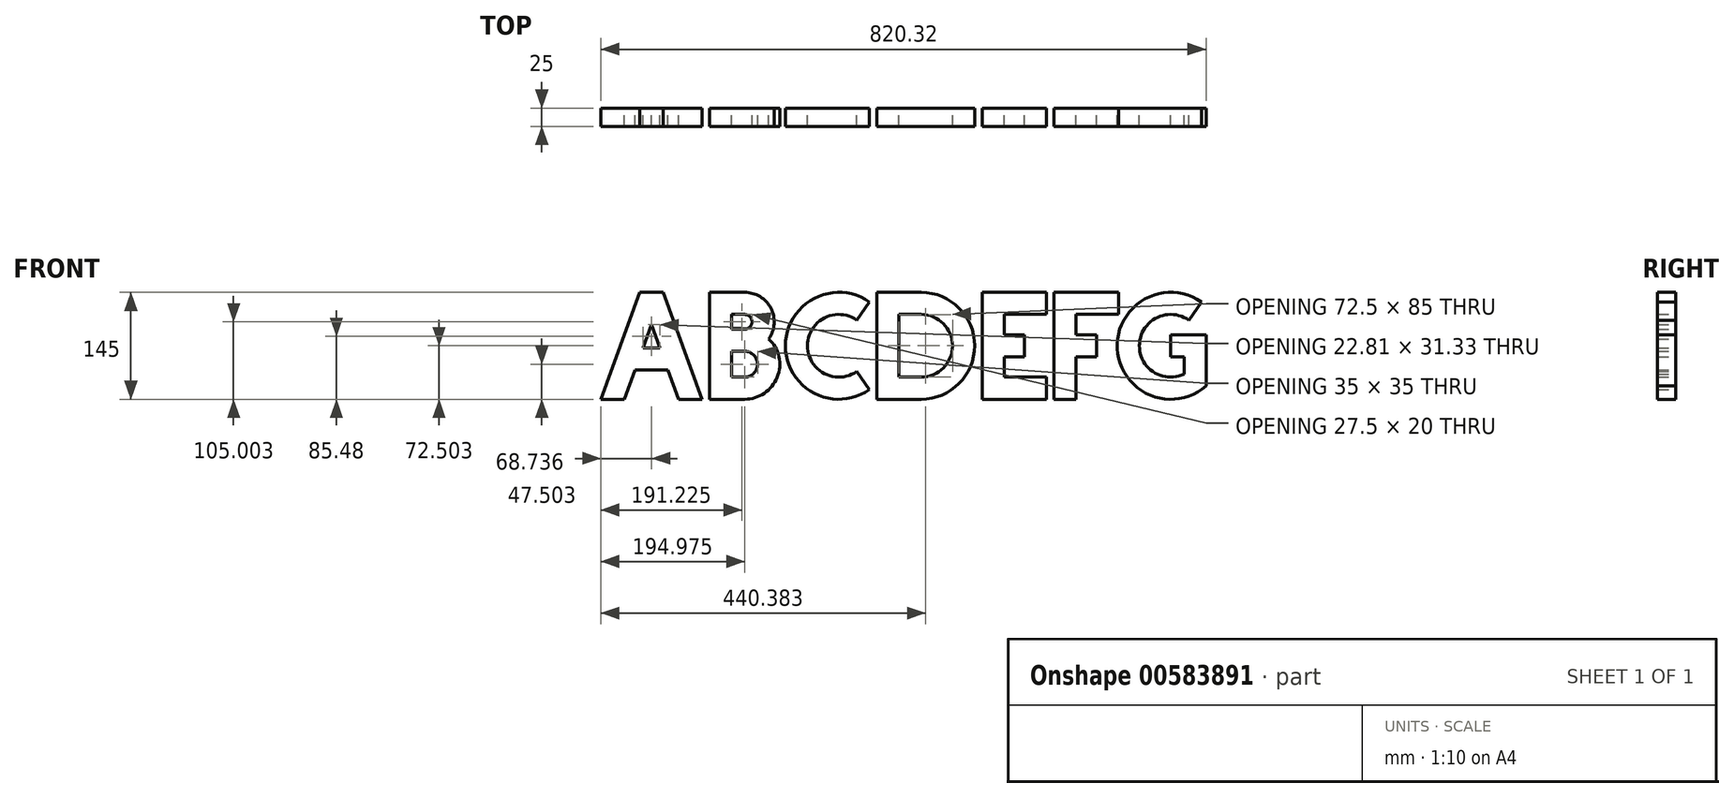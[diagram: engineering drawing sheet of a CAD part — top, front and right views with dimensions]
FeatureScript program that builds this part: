
annotation { "Feature Type Name" : "Feature", "Feature Type Description" : "" }
export const myFeature = defineFeature(function(context is Context, id is Id, definition is map)
    precondition{}
    {
        {
            var Q0;
            Q0=qCreatedBy(makeId("Front.planeOp"),FACE);
            var sketch = newSketch(context, id + "F0", { "sketchPlane" : qUnion([Q0])});
            skLineSegment(sketch, "E0", {"start": v(-189.1, -161.69) * mm, "end": v(-189.1, -191.69) * mm, "construction": true});
            skLineSegment(sketch, "E1", {"start": v(-189.1, -161.69) * mm, "end": v(-189.1, -96.69) * mm, "construction": true});
            skLineSegment(sketch, "E2", {"start": v(-189.1, -46.69) * mm, "end": v(-189.1, -96.69) * mm, "construction": true});
            skLineSegment(sketch, "E3", {"start": v(-179.1, -191.69) * mm, "end": v(-126.33, -46.69) * mm});
            skLineSegment(sketch, "E4", {"start": v(-126.33, -46.69) * mm, "end": v(-94.4, -46.69) * mm});
            skLineSegment(sketch, "E5", {"start": v(-94.4, -46.69) * mm, "end": v(-41.63, -191.69) * mm});
            skLineSegment(sketch, "E6", {"start": v(-41.63, -191.69) * mm, "end": v(-73.55, -191.69) * mm});
            skLineSegment(sketch, "E7", {"start": v(-73.55, -191.69) * mm, "end": v(-88.04, -151.88) * mm});
            skLineSegment(sketch, "E8", {"start": v(-88.04, -151.88) * mm, "end": v(-132.69, -151.88) * mm});
            skLineSegment(sketch, "E9", {"start": v(-132.69, -151.88) * mm, "end": v(-147.18, -191.69) * mm});
            skLineSegment(sketch, "E10", {"start": v(-147.18, -191.69) * mm, "end": v(-179.1, -191.69) * mm});
            skLineSegment(sketch, "E11", {"start": v(-121.77, -121.88) * mm, "end": v(-110.36, -90.54) * mm});
            skLineSegment(sketch, "E12", {"start": v(-110.36, -90.54) * mm, "end": v(-98.96, -121.88) * mm});
            skLineSegment(sketch, "E13", {"start": v(-98.96, -121.88) * mm, "end": v(-121.77, -121.88) * mm});
            skPoint(sketch, "E14", {"position": v(-110.36, -121.88) * mm});
            skPoint(sketch, "E15", {"position": v(-110.36, -151.88) * mm});
            skLineSegment(sketch, "E16", {"start": v(-110.36, -121.88) * mm, "end": v(-110.36, -151.88) * mm, "construction": true});
            skLineSegment(sketch, "E17", {"start": v(-179.1, -46.69) * mm, "end": v(-179.1, -191.69) * mm, "construction": true});
            skLineSegment(sketch, "E18", {"start": v(-189.1, -191.69) * mm, "end": v(-179.1, -191.69) * mm, "construction": true});
            skLineSegment(sketch, "E19", {"start": v(-31.63, -46.69) * mm, "end": v(-31.63, -191.69) * mm});
            skLineSegment(sketch, "E20", {"start": v(-31.63, -191.69) * mm, "end": v(15.87, -191.69) * mm});
            skArc(sketch, "E21", {"start": v(15.87, -191.69) * mm, "mid": v(60, -161.79) * mm, "end": v(48.57, -109.73) * mm});
            skArc(sketch, "E22", {"start": v(48.57, -109.73) * mm, "mid": v(51.38, -68.27) * mm, "end": v(15.87, -46.69) * mm});
            skLineSegment(sketch, "E23", {"start": v(15.87, -46.69) * mm, "end": v(-31.63, -46.69) * mm});
            skLineSegment(sketch, "E24", {"start": v(-41.63, -191.69) * mm, "end": v(-31.63, -191.69) * mm, "construction": true});
            skLineSegment(sketch, "E25", {"start": v(-139.93, -171.78) * mm, "end": v(-168.12, -161.52) * mm, "construction": true});
            skLineSegment(sketch, "E26", {"start": v(15.87, -76.69) * mm, "end": v(-1.63, -76.69) * mm});
            skLineSegment(sketch, "E27", {"start": v(-1.63, -76.69) * mm, "end": v(-1.63, -96.69) * mm});
            skLineSegment(sketch, "E28", {"start": v(-1.63, -96.69) * mm, "end": v(15.87, -96.69) * mm});
            skArc(sketch, "E29", {"start": v(15.87, -96.69) * mm, "mid": v(25.87, -86.69) * mm, "end": v(15.87, -76.69) * mm});
            skLineSegment(sketch, "E30", {"start": v(15.87, -126.69) * mm, "end": v(-1.63, -126.69) * mm});
            skLineSegment(sketch, "E31", {"start": v(-1.63, -126.69) * mm, "end": v(-1.63, -161.69) * mm});
            skLineSegment(sketch, "E32", {"start": v(-1.63, -161.69) * mm, "end": v(15.87, -161.69) * mm});
            skArc(sketch, "E33", {"start": v(15.87, -161.69) * mm, "mid": v(33.37, -144.19) * mm, "end": v(15.87, -126.69) * mm});
            skLineSegment(sketch, "E34", {"start": v(15.87, -161.69) * mm, "end": v(15.87, -191.69) * mm, "construction": true});
            skLineSegment(sketch, "E35", {"start": v(15.87, -96.69) * mm, "end": v(15.87, -126.69) * mm, "construction": true});
            skLineSegment(sketch, "E36", {"start": v(15.87, -46.69) * mm, "end": v(15.87, -76.69) * mm, "construction": true});
            skLineSegment(sketch, "E37", {"start": v(-1.63, -144.19) * mm, "end": v(-31.63, -144.19) * mm, "construction": true});
            skArc(sketch, "E38", {"start": v(185.03, -59.8) * mm, "mid": v(70.95, -119.19) * mm, "end": v(185.03, -178.58) * mm});
            skArc(sketch, "E39", {"start": v(167.83, -84.37) * mm, "mid": v(100.95, -119.19) * mm, "end": v(167.83, -154) * mm});
            skLineSegment(sketch, "E40", {"start": v(167.83, -84.37) * mm, "end": v(185.03, -59.8) * mm});
            skLineSegment(sketch, "E41", {"start": v(167.83, -154) * mm, "end": v(185.03, -178.58) * mm});
            skLineSegment(sketch, "E42", {"start": v(72.3, -133.13) * mm, "end": v(62.49, -135.05) * mm, "construction": true});
            skLineSegment(sketch, "E43", {"start": v(143.45, -119.19) * mm, "end": v(143.45, -191.69) * mm, "construction": true});
            skPoint(sketch, "E44", {"position": v(143.45, -46.69) * mm});
            skLineSegment(sketch, "E45", {"start": v(143.45, -46.69) * mm, "end": v(143.45, -119.19) * mm, "construction": true});
            skLineSegment(sketch, "E46", {"start": v(195.03, -46.69) * mm, "end": v(195.03, -191.69) * mm});
            skLineSegment(sketch, "E47", {"start": v(195.03, -191.69) * mm, "end": v(255.03, -191.69) * mm});
            skLineSegment(sketch, "E48", {"start": v(195.03, -46.69) * mm, "end": v(255.03, -46.69) * mm});
            skArc(sketch, "E49", {"start": v(255.03, -46.69) * mm, "mid": v(327.53, -119.19) * mm, "end": v(255.03, -191.69) * mm});
            skLineSegment(sketch, "E50", {"start": v(255.03, -76.69) * mm, "end": v(225.03, -76.69) * mm});
            skLineSegment(sketch, "E51", {"start": v(225.03, -76.69) * mm, "end": v(225.03, -161.69) * mm});
            skLineSegment(sketch, "E52", {"start": v(225.03, -161.69) * mm, "end": v(255.03, -161.69) * mm});
            skLineSegment(sketch, "E53", {"start": v(225.03, -119.19) * mm, "end": v(195.03, -119.19) * mm, "construction": true});
            skArc(sketch, "E54", {"start": v(255.03, -76.69) * mm, "mid": v(297.53, -119.19) * mm, "end": v(255.03, -161.69) * mm});
            skLineSegment(sketch, "E55", {"start": v(255.03, -46.69) * mm, "end": v(255.03, -76.69) * mm, "construction": true});
            skLineSegment(sketch, "E56", {"start": v(255.03, -161.69) * mm, "end": v(255.03, -191.69) * mm, "construction": true});
            skLineSegment(sketch, "E57", {"start": v(185.03, -178.58) * mm, "end": v(195.03, -178.58) * mm, "construction": true});
            skLineSegment(sketch, "E58", {"start": v(15.87, -144.19) * mm, "end": v(33.37, -144.19) * mm, "construction": true});
            skLineSegment(sketch, "E59", {"start": v(-1.63, -144.19) * mm, "end": v(15.87, -144.19) * mm, "construction": true});
            skLineSegment(sketch, "E60", {"start": v(337.53, -46.69) * mm, "end": v(337.53, -191.69) * mm});
            skLineSegment(sketch, "E61", {"start": v(337.53, -191.69) * mm, "end": v(425.03, -191.69) * mm});
            skLineSegment(sketch, "E62", {"start": v(425.03, -191.69) * mm, "end": v(425.03, -161.69) * mm});
            skLineSegment(sketch, "E63", {"start": v(425.03, -161.69) * mm, "end": v(395.03, -161.69) * mm});
            skLineSegment(sketch, "E64", {"start": v(367.53, -161.69) * mm, "end": v(367.53, -134.19) * mm});
            skLineSegment(sketch, "E65", {"start": v(367.53, -134.19) * mm, "end": v(395.03, -134.19) * mm});
            skLineSegment(sketch, "E66", {"start": v(395.03, -134.19) * mm, "end": v(395.03, -104.19) * mm});
            skLineSegment(sketch, "E67", {"start": v(395.03, -104.19) * mm, "end": v(367.53, -104.19) * mm});
            skLineSegment(sketch, "E68", {"start": v(367.53, -104.19) * mm, "end": v(367.53, -76.69) * mm});
            skLineSegment(sketch, "E69", {"start": v(367.53, -76.69) * mm, "end": v(395.03, -76.69) * mm});
            skLineSegment(sketch, "E70", {"start": v(425.03, -76.69) * mm, "end": v(425.03, -46.69) * mm});
            skLineSegment(sketch, "E71", {"start": v(425.03, -46.69) * mm, "end": v(337.53, -46.69) * mm});
            skLineSegment(sketch, "E72", {"start": v(327.53, -119.19) * mm, "end": v(337.53, -119.19) * mm, "construction": true});
            skLineSegment(sketch, "E73", {"start": v(367.53, -90.44) * mm, "end": v(337.53, -90.44) * mm, "construction": true});
            skLineSegment(sketch, "E74", {"start": v(395.03, -76.69) * mm, "end": v(425.03, -76.69) * mm});
            skLineSegment(sketch, "E75", {"start": v(395.03, -161.69) * mm, "end": v(367.53, -161.69) * mm});
            skLineSegment(sketch, "E76", {"start": v(435.03, -46.69) * mm, "end": v(435.03, -191.69) * mm});
            skLineSegment(sketch, "E77", {"start": v(435.03, -191.69) * mm, "end": v(465.03, -191.69) * mm});
            skLineSegment(sketch, "E78", {"start": v(465.03, -191.69) * mm, "end": v(465.03, -161.69) * mm});
            skLineSegment(sketch, "E79", {"start": v(465.03, -134.19) * mm, "end": v(492.53, -134.19) * mm});
            skLineSegment(sketch, "E80", {"start": v(492.53, -134.19) * mm, "end": v(492.53, -104.19) * mm});
            skLineSegment(sketch, "E81", {"start": v(492.53, -104.19) * mm, "end": v(465.03, -104.19) * mm});
            skLineSegment(sketch, "E82", {"start": v(465.03, -104.19) * mm, "end": v(465.03, -76.69) * mm});
            skLineSegment(sketch, "E83", {"start": v(465.03, -76.69) * mm, "end": v(492.53, -76.69) * mm});
            skLineSegment(sketch, "E84", {"start": v(522.53, -76.69) * mm, "end": v(522.53, -46.69) * mm});
            skLineSegment(sketch, "E85", {"start": v(522.53, -46.69) * mm, "end": v(435.03, -46.69) * mm});
            skLineSegment(sketch, "E86", {"start": v(465.03, -161.69) * mm, "end": v(465.03, -134.19) * mm});
            skLineSegment(sketch, "E87", {"start": v(492.53, -76.69) * mm, "end": v(522.53, -76.69) * mm});
            skLineSegment(sketch, "E88", {"start": v(425.03, -176.69) * mm, "end": v(435.03, -176.69) * mm, "construction": true});
            skArc(sketch, "E89", {"start": v(634.83, -59.8) * mm, "mid": v(520.86, -123.26) * mm, "end": v(641.22, -173.54) * mm});
            skLineSegment(sketch, "E90", {"start": v(634.83, -59.8) * mm, "end": v(617.62, -84.37) * mm});
            skArc(sketch, "E91", {"start": v(617.62, -84.37) * mm, "mid": v(550.9, -115.5) * mm, "end": v(611.22, -157.7) * mm});
            skLineSegment(sketch, "E92", {"start": v(611.22, -157.7) * mm, "end": v(611.22, -134.19) * mm});
            skLineSegment(sketch, "E93", {"start": v(611.22, -134.19) * mm, "end": v(593.24, -134.19) * mm});
            skLineSegment(sketch, "E94", {"start": v(593.24, -134.19) * mm, "end": v(593.24, -104.19) * mm});
            skLineSegment(sketch, "E95", {"start": v(593.24, -104.19) * mm, "end": v(641.22, -104.19) * mm});
            skLineSegment(sketch, "E96", {"start": v(641.22, -104.19) * mm, "end": v(641.22, -173.54) * mm});
            skPoint(sketch, "E97", {"position": v(593.24, -46.69) * mm});
            skPoint(sketch, "E98", {"position": v(593.24, -191.69) * mm});
            skLineSegment(sketch, "E99", {"start": v(522.53, -76.69) * mm, "end": v(531.1, -81.84) * mm, "construction": true});
            skLineSegment(sketch, "E100", {"start": v(611.22, -145.94) * mm, "end": v(641.22, -145.94) * mm, "construction": true});
            skPoint(sketch, "E101", {"position": v(626.22, -145.94) * mm});
            skPoint(sketch, "E102", {"position": v(626.22, -72.09) * mm});
            skSolve(sketch);
        }
        {
            var Q0;
            Q0=makeQuery(id+"F0.imprint","IMPRINT",FACE,{"disambiguationData":[TD([[makeQuery(id+"F0.imprint","IMPRINT",EDGE,{"derivedFrom":sQuery(id+"F0.wireOp",EDGE,"E3")}),-1.0]])]});
            var Q1;
            Q1=makeQuery(id+"F0.imprint","IMPRINT",FACE,{"disambiguationData":[TD([[makeQuery(id+"F0.imprint","IMPRINT",EDGE,{"derivedFrom":sQuery(id+"F0.wireOp",EDGE,"E19")}),1.0]])]});
            var Q2;
            Q2=makeQuery(id+"F0.imprint","IMPRINT",FACE,{"disambiguationData":[TD([[makeQuery(id+"F0.imprint","IMPRINT",EDGE,{"derivedFrom":sQuery(id+"F0.wireOp",EDGE,"E38")}),1.0]])]});
            var Q3;
            Q3=makeQuery(id+"F0.imprint","IMPRINT",FACE,{"disambiguationData":[TD([[makeQuery(id+"F0.imprint","IMPRINT",EDGE,{"derivedFrom":sQuery(id+"F0.wireOp",EDGE,"E46")}),1.0]])]});
            var Q4;
            Q4=makeQuery(id+"F0.imprint","IMPRINT",FACE,{"disambiguationData":[TD([[makeQuery(id+"F0.imprint","IMPRINT",EDGE,{"derivedFrom":sQuery(id+"F0.wireOp",EDGE,"E60")}),1.0]])]});
            var Q5;
            Q5=makeQuery(id+"F0.imprint","IMPRINT",FACE,{"disambiguationData":[TD([[makeQuery(id+"F0.imprint","IMPRINT",EDGE,{"derivedFrom":sQuery(id+"F0.wireOp",EDGE,"E76")}),1.0]])]});
            var Q6;
            Q6=makeQuery(id+"F0.imprint","IMPRINT",FACE,{"disambiguationData":[TD([[makeQuery(id+"F0.imprint","IMPRINT",EDGE,{"derivedFrom":sQuery(id+"F0.wireOp",EDGE,"E89")}),1.0]])]});
            extrude(context, id + "F1", {"entities" : qUnion([Q0, Q1, Q2, Q3, Q4, Q5, Q6]), "depth" : 25 * mm, "offsetDistance" : 25 * mm});
        }
    });
